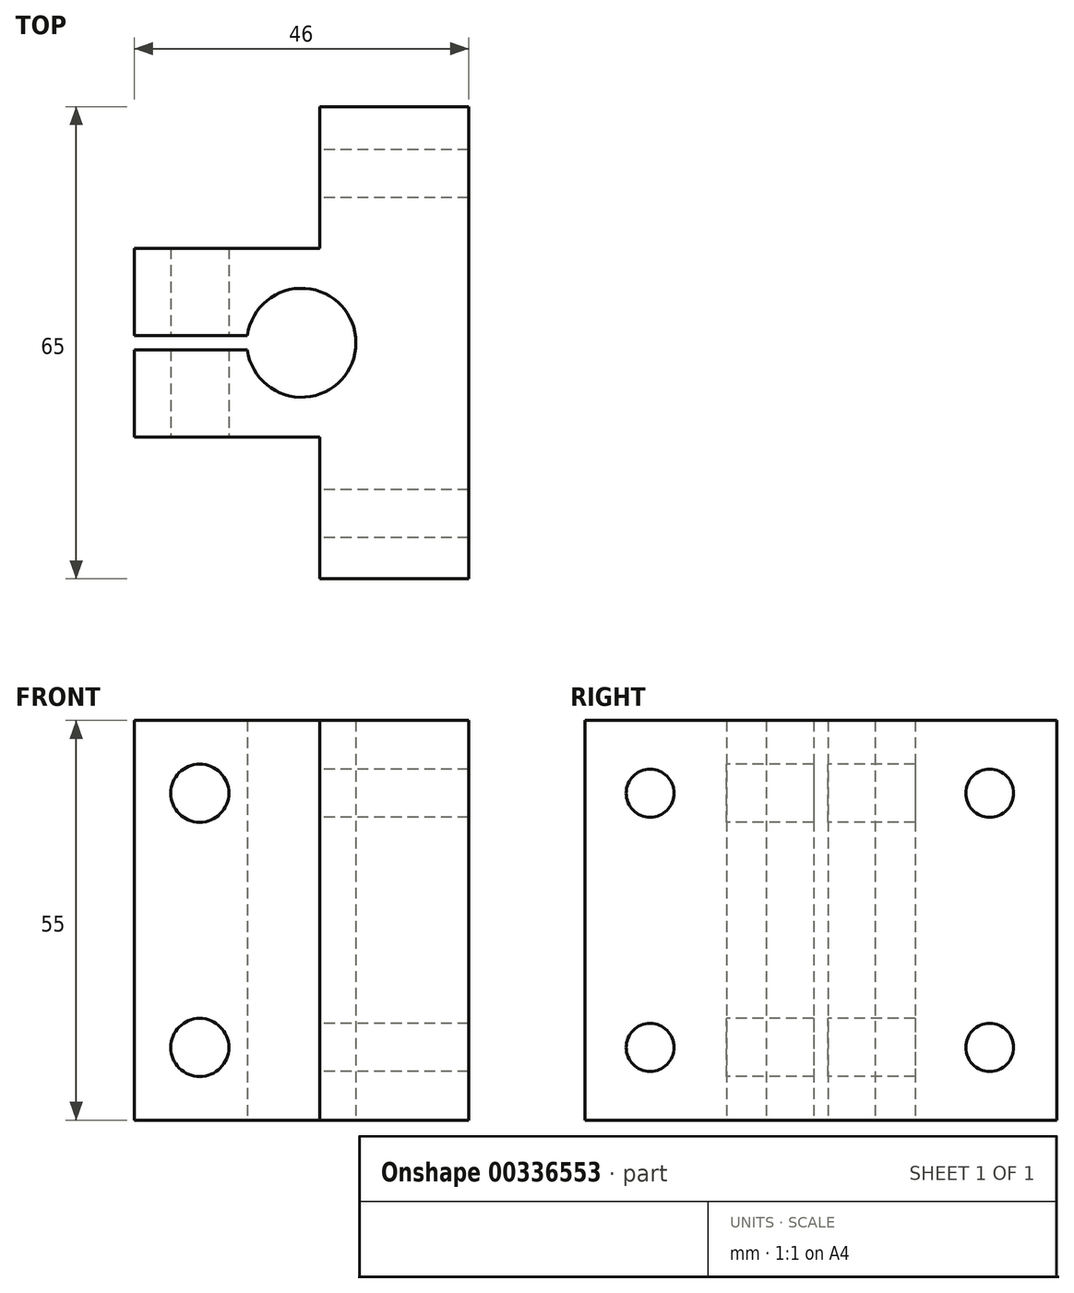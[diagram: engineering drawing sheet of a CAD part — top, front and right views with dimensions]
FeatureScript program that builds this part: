
annotation { "Feature Type Name" : "Feature", "Feature Type Description" : "" }
export const myFeature = defineFeature(function(context is Context, id is Id, definition is map)
    precondition{}
    {
        {
            var Q0;
            Q0=qCreatedBy(makeId("Top.planeOp"),FACE);
            var sketch = newSketch(context, id + "F0", { "sketchPlane" : qUnion([Q0])});
            skLineSegment(sketch, "E0", {"start": v(0, 0) * mm, "end": v(20.5, 0) * mm});
            skLineSegment(sketch, "E1", {"start": v(20.5, 0) * mm, "end": v(20.5, -65) * mm});
            skLineSegment(sketch, "E2", {"start": v(20.5, -65) * mm, "end": v(0, -65) * mm});
            skLineSegment(sketch, "E3", {"start": v(0, -65) * mm, "end": v(0, -45.5) * mm});
            skLineSegment(sketch, "E4", {"start": v(0, -45.5) * mm, "end": v(-25.5, -45.5) * mm});
            skLineSegment(sketch, "E5", {"start": v(-25.5, -45.5) * mm, "end": v(-25.5, -33.5) * mm});
            skLineSegment(sketch, "E6", {"start": v(-25.5, -33.5) * mm, "end": v(-9.93, -33.5) * mm});
            skLineSegment(sketch, "E7", {"start": v(-9.93, -31.5) * mm, "end": v(-25.5, -31.5) * mm});
            skLineSegment(sketch, "E8", {"start": v(-25.5, -31.5) * mm, "end": v(-25.5, -19.5) * mm});
            skLineSegment(sketch, "E9", {"start": v(-25.5, -19.5) * mm, "end": v(0, -19.5) * mm});
            skLineSegment(sketch, "E10", {"start": v(0, -19.5) * mm, "end": v(0, 0) * mm});
            skArc(sketch, "E11", {"start": v(-9.93, -33.5) * mm, "mid": v(5, -32.5) * mm, "end": v(-9.93, -31.5) * mm});
            skSolve(sketch);
        }
        {
            var Q0;
            Q0 = qSketchRegion(id + "F0", true);
            extrude(context, id + "F1", {"entities" : qUnion([Q0]), "depth" : 55 * mm});
        }
        {
            var Q0;
            Q0=makeQuery(id+"F1.opExtrude","SWEPT_FACE",FACE,{"disambiguationData":[OSD([sQuery(id+"F0.wireOp",EDGE,"E4")])]});
            cPlane(context, id + "F2", {"entities" : qUnion([Q0]), "cplaneType" : CPlaneType.OFFSET, "offset" : 0 * mm, "width" : 150 * mm, "height" : 150 * mm});
        }
        {
            var Q0;
            Q0=qCreatedBy(id+"F2.planeOp",FACE);
            var sketch = newSketch(context, id + "F3", { "sketchPlane" : qUnion([Q0])});
            skCircle(sketch, "E12", {"center": v(-16.5, 10) * mm, "radius": 4 * mm});
            skSolve(sketch);
        }
        {
            var Q0;
            Q0 = qSketchRegion(id + "F3", true);
            extrude(context, id + "F4", {"entities" : qUnion([Q0]), "operationType" : NewBodyOperationType.REMOVE, "endBound" : BoundingType.SYMMETRIC, "oppositeDirection" : true, "depth" : 100 * mm});
        }
        {
            var Q0;
            Q0=qCreatedBy(id+"F2.planeOp",FACE);
            var sketch = newSketch(context, id + "F5", { "sketchPlane" : qUnion([Q0])});
            skLineSegment(sketch, "E13", {"start": v(0, 0) * mm, "end": v(0, 55) * mm});
            skLineSegment(sketch, "E14", {"start": v(0, 55) * mm, "end": v(-25.5, 55) * mm});
            skCircle(sketch, "E15", {"center": v(-16.5, 45) * mm, "radius": 4 * mm});
            skSolve(sketch);
        }
        {
            var Q0;
            Q0 = qSketchRegion(id + "F5", true);
            extrude(context, id + "F6", {"entities" : qUnion([Q0]), "operationType" : NewBodyOperationType.REMOVE, "oppositeDirection" : true, "depth" : 100 * mm});
        }
        {
            var Q0;
            Q0=makeQuery(id+"F1.opExtrude","SWEPT_FACE",FACE,{"disambiguationData":[OSD([sQuery(id+"F0.wireOp",EDGE,"E3")])]});
            cPlane(context, id + "F7", {"entities" : qUnion([Q0]), "cplaneType" : CPlaneType.OFFSET, "offset" : 0 * mm, "width" : 150 * mm, "height" : 150 * mm});
        }
        {
            var Q0;
            Q0=qCreatedBy(id+"F7.planeOp",FACE);
            var sketch = newSketch(context, id + "F8", { "sketchPlane" : qUnion([Q0])});
            skCircle(sketch, "E16", {"center": v(9.25, 45) * mm, "radius": 3.3 * mm});
            skCircle(sketch, "E17", {"center": v(9.25, 10) * mm, "radius": 3.3 * mm});
            skSolve(sketch);
        }
        {
            var Q0;
            Q0 = qSketchRegion(id + "F8", true);
            extrude(context, id + "F9", {"entities" : qUnion([Q0]), "operationType" : NewBodyOperationType.REMOVE, "oppositeDirection" : true, "depth" : 25 * mm});
        }
        {
            var Q0;
            Q0=qCreatedBy(id+"F7.planeOp",FACE);
            var sketch = newSketch(context, id + "F10", { "sketchPlane" : qUnion([Q0])});
            skCircle(sketch, "E18", {"center": v(56, 10) * mm, "radius": 3.3 * mm});
            skCircle(sketch, "E19", {"center": v(56, 45) * mm, "radius": 3.3 * mm});
            skSolve(sketch);
        }
        {
            var Q0;
            Q0 = qSketchRegion(id + "F10", true);
            extrude(context, id + "F11", {"entities" : qUnion([Q0]), "operationType" : NewBodyOperationType.REMOVE, "oppositeDirection" : true, "depth" : 25 * mm});
        }
    });
